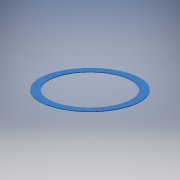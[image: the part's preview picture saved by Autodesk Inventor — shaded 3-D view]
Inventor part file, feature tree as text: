
AUTODESK INVENTOR PART (.ipt)
format: ipt  version: 2018 (Build 220112000, 112)  size: 100,864 bytes
history: native  units: mm
features: extrude x1, sketch x1
ambient origin geometry x8: Origin, YZ Plane, XZ Plane, XY Plane, X Axis, Y Axis, Z Axis, Center Point
bodies: Solid1 (feature_tree)
feature tree (2):
  extrude  "Extrusion1"  Depth=0.2mm
  sketch  "Sketch1"  dims[d0=29.0mm d1=24.0mm d2=0.2mm d3=0.0mm]
